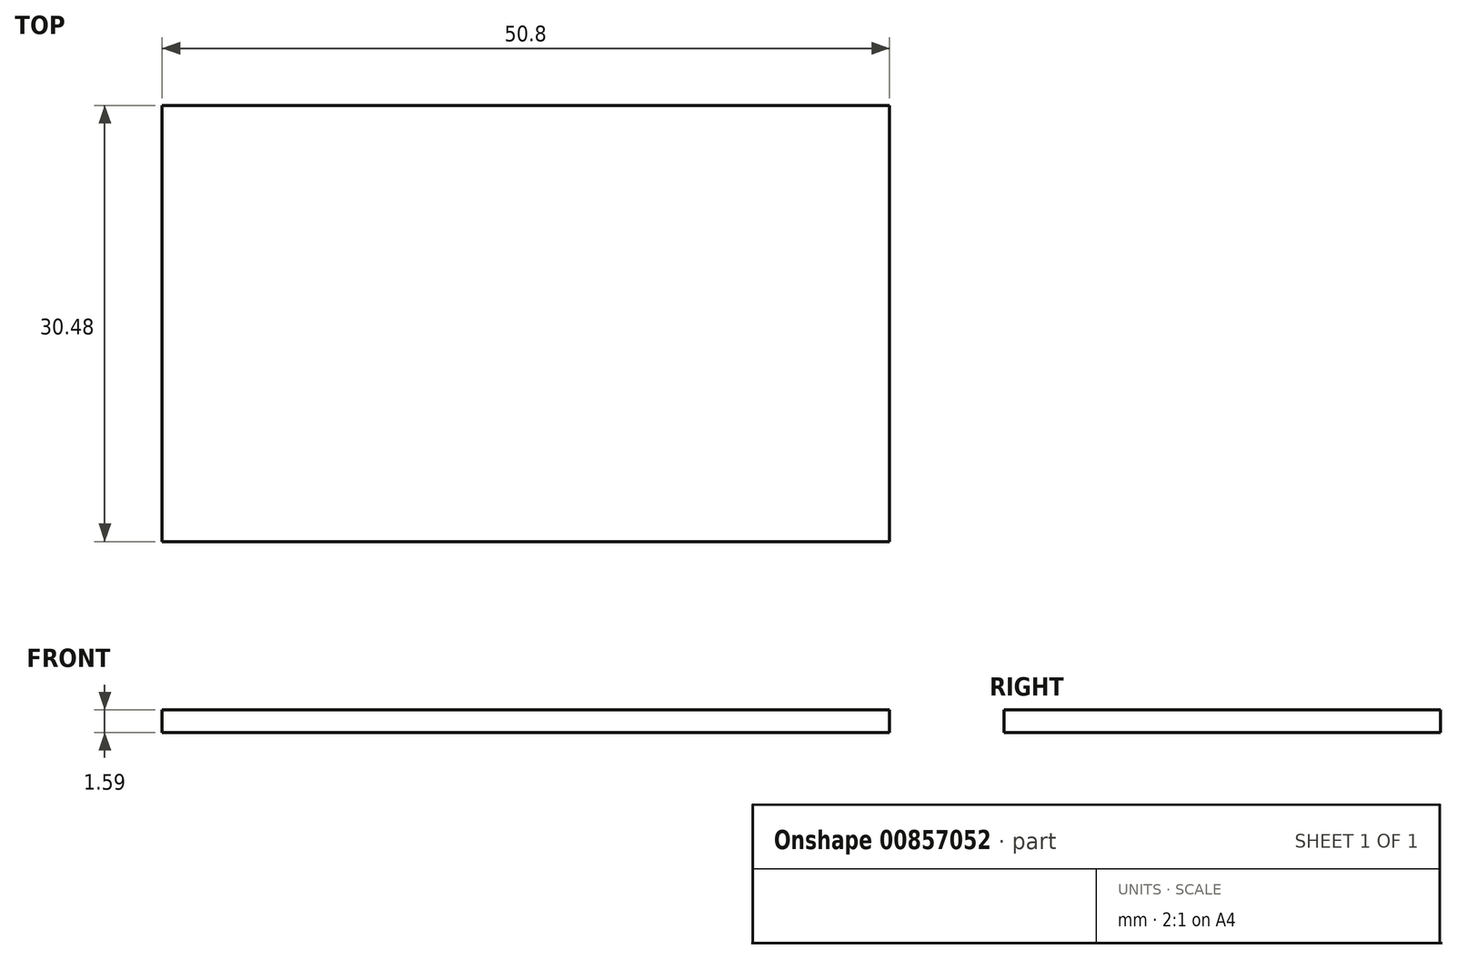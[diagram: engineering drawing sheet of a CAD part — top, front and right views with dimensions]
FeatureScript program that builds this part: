
annotation { "Feature Type Name" : "Feature", "Feature Type Description" : "" }
export const myFeature = defineFeature(function(context is Context, id is Id, definition is map)
    precondition{}
    {
        {
            var Q0;
            Q0=qCreatedBy(makeId("Top.planeOp"),FACE);
            var sketch = newSketch(context, id + "F0", { "sketchPlane" : qUnion([Q0])});
            skLineSegment(sketch, "E0.bottom", {"start": v(-25.4, 15.24) * mm, "end": v(25.4, 15.24) * mm});
            skLineSegment(sketch, "E0.top", {"start": v(-25.4, -15.24) * mm, "end": v(25.4, -15.24) * mm});
            skLineSegment(sketch, "E0.left", {"start": v(-25.4, 15.24) * mm, "end": v(-25.4, -15.24) * mm});
            skLineSegment(sketch, "E0.right", {"start": v(25.4, 15.24) * mm, "end": v(25.4, -15.24) * mm});
            skPoint(sketch, "E0.middle", {"position": v(0, 0) * mm});
            skSolve(sketch);
        }
        {
            var Q0;
            Q0 = qSketchRegion(id + "F0", true);
            extrude(context, id + "F1", {"entities" : qUnion([Q0]), "depth" : 1.59 * mm, "offsetDistance" : 25.4 * mm});
        }
    });
